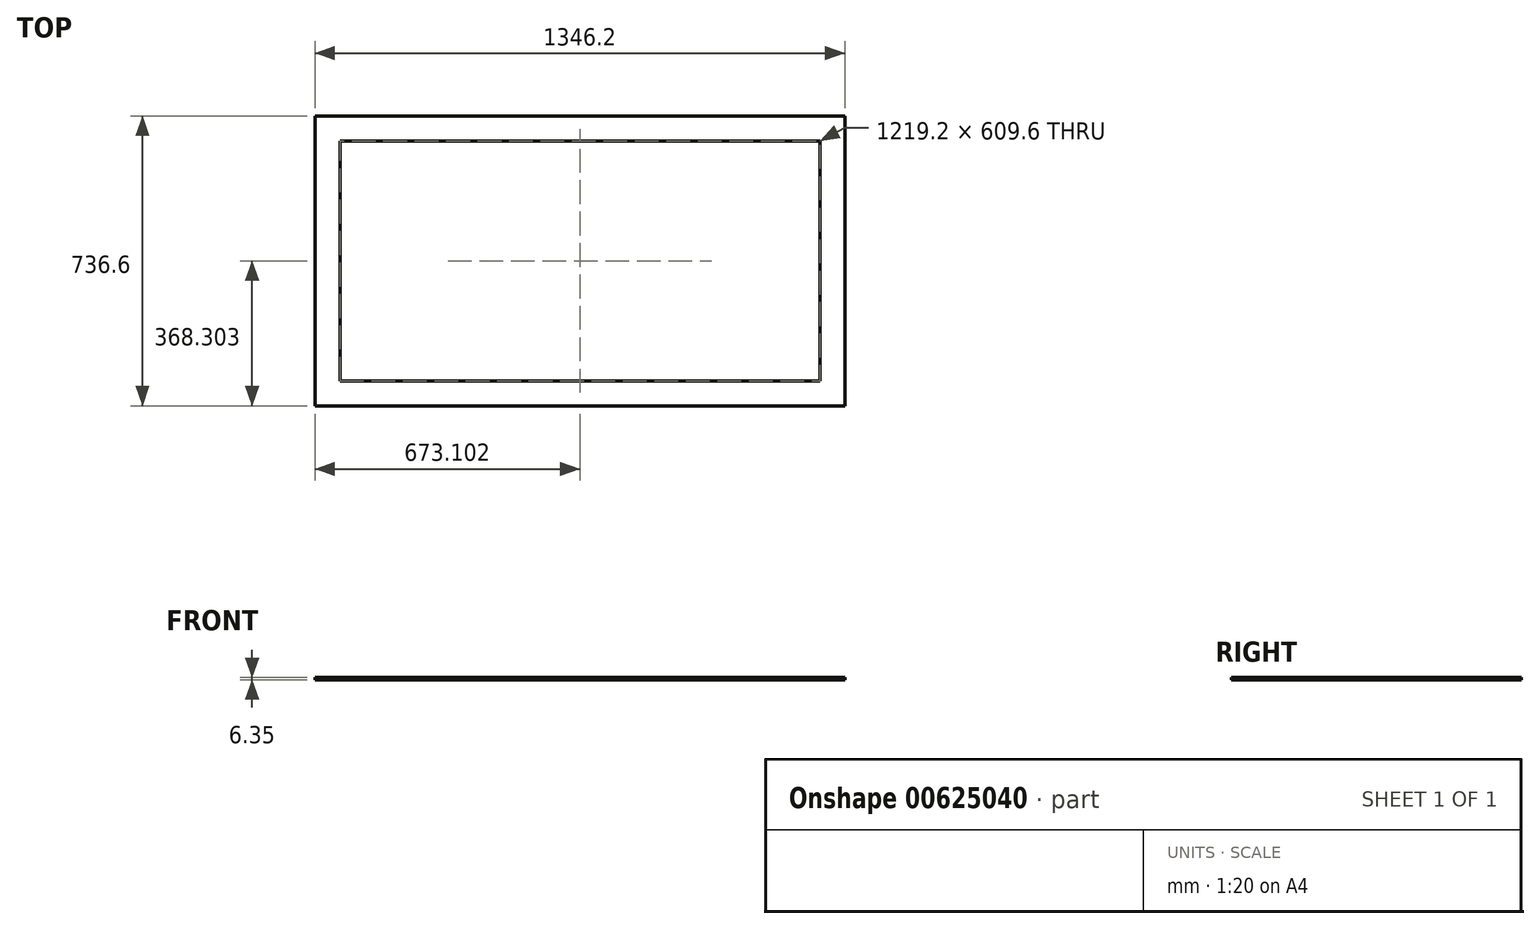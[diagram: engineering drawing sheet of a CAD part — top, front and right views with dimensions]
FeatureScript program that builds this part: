
annotation { "Feature Type Name" : "Feature", "Feature Type Description" : "" }
export const myFeature = defineFeature(function(context is Context, id is Id, definition is map)
    precondition{}
    {
        {
            var Q0;
            Q0=qCreatedBy(makeId("Top.planeOp"),FACE);
            var sketch = newSketch(context, id + "F0", { "sketchPlane" : qUnion([Q0])});
            skLineSegment(sketch, "E0.bottom", {"start": v(-1280.33, 1209.42) * mm, "end": v(-61.13, 1209.42) * mm});
            skLineSegment(sketch, "E0.top", {"start": v(-1280.33, 599.82) * mm, "end": v(-61.13, 599.82) * mm});
            skLineSegment(sketch, "E0.left", {"start": v(-1280.33, 1209.42) * mm, "end": v(-1280.33, 599.82) * mm});
            skLineSegment(sketch, "E0.right", {"start": v(-61.13, 1209.42) * mm, "end": v(-61.13, 599.82) * mm});
            skLineSegment(sketch, "E1.0", {"start": v(-1343.83, 1272.92) * mm, "end": v(2.37, 1272.92) * mm});
            skLineSegment(sketch, "E1.1", {"start": v(-1343.83, 1272.92) * mm, "end": v(-1343.83, 536.32) * mm});
            skLineSegment(sketch, "E1.2", {"start": v(-1343.83, 536.32) * mm, "end": v(2.37, 536.32) * mm});
            skLineSegment(sketch, "E1.3", {"start": v(2.37, 1272.92) * mm, "end": v(2.37, 536.32) * mm});
            skLineSegment(sketch, "E2", {"start": v(-1280.33, 599.82) * mm, "end": v(-1280.33, 536.32) * mm});
            skLineSegment(sketch, "E3", {"start": v(-61.13, 599.82) * mm, "end": v(-61.13, 536.32) * mm});
            skLineSegment(sketch, "E4", {"start": v(-61.13, 1209.42) * mm, "end": v(-61.13, 1272.92) * mm});
            skLineSegment(sketch, "E5", {"start": v(-1280.33, 1209.42) * mm, "end": v(-1280.33, 1272.92) * mm});
            skLineSegment(sketch, "E6", {"start": v(-1280.33, 599.82) * mm, "end": v(-1343.83, 599.82) * mm});
            skLineSegment(sketch, "E7", {"start": v(-61.13, 1209.42) * mm, "end": v(0, 1209.42) * mm});
            skLineSegment(sketch, "E8", {"start": v(-61.13, 599.82) * mm, "end": v(0, 599.82) * mm});
            skLineSegment(sketch, "E9", {"start": v(-1280.33, 1209.42) * mm, "end": v(-1343.83, 1209.42) * mm});
            skSolve(sketch);
        }
        {
            var Q0;
            {var subQ3=sQuery(id+"F0.wireOp",EDGE,"E5");Q0=makeQuery(id+"F0.imprint","IMPRINT",FACE,{"disambiguationData":[TD([[makeQuery(id+"F0.imprint","IMPRINT",EDGE,{"derivedFrom":subQ3}),1.0]])]});}
            var Q1;
            {var subQ4=sQuery(id+"F0.wireOp",EDGE,"E2");Q1=makeQuery(id+"F0.imprint","IMPRINT",FACE,{"disambiguationData":[TD([[makeQuery(id+"F0.imprint","IMPRINT",EDGE,{"derivedFrom":subQ4}),-1.0]])]});}
            var Q2;
            Q2=makeQuery(id+"F0.imprint","IMPRINT",FACE,{"disambiguationData":[TD([[makeQuery(id+"F0.imprint","IMPRINT",EDGE,{"derivedFrom":sQuery(id+"F0.wireOp",EDGE,"E0.bottom")}),1.0]])]});
            var Q3;
            Q3=makeQuery(id+"F0.imprint","IMPRINT",FACE,{"disambiguationData":[TD([[makeQuery(id+"F0.imprint","IMPRINT",EDGE,{"derivedFrom":sQuery(id+"F0.wireOp",EDGE,"E0.top")}),-1.0]])]});
            var Q4;
            Q4=makeQuery(id+"F0.imprint","IMPRINT",FACE,{"disambiguationData":[TD([[makeQuery(id+"F0.imprint","IMPRINT",EDGE,{"derivedFrom":sQuery(id+"F0.wireOp",EDGE,"E0.right")}),1.0]])]});
            extrude(context, id + "F1", {"entities" : qUnion([Q0, Q1, Q2, Q3, Q4]), "depth" : 6.35 * mm, "offsetDistance" : 25.4 * mm});
        }
        {
            var Q0;
            Q0=makeQuery(id+"F0.imprint","IMPRINT",FACE,{"disambiguationData":[TD([[makeQuery(id+"F0.imprint","IMPRINT",EDGE,{"derivedFrom":sQuery(id+"F0.wireOp",EDGE,"E0.left")}),-1.0]])]});
            extrude(context, id + "F2", {"entities" : qUnion([Q0]), "operationType" : NewBodyOperationType.ADD, "depth" : 6.35 * mm, "offsetDistance" : 25.4 * mm});
        }
    });
